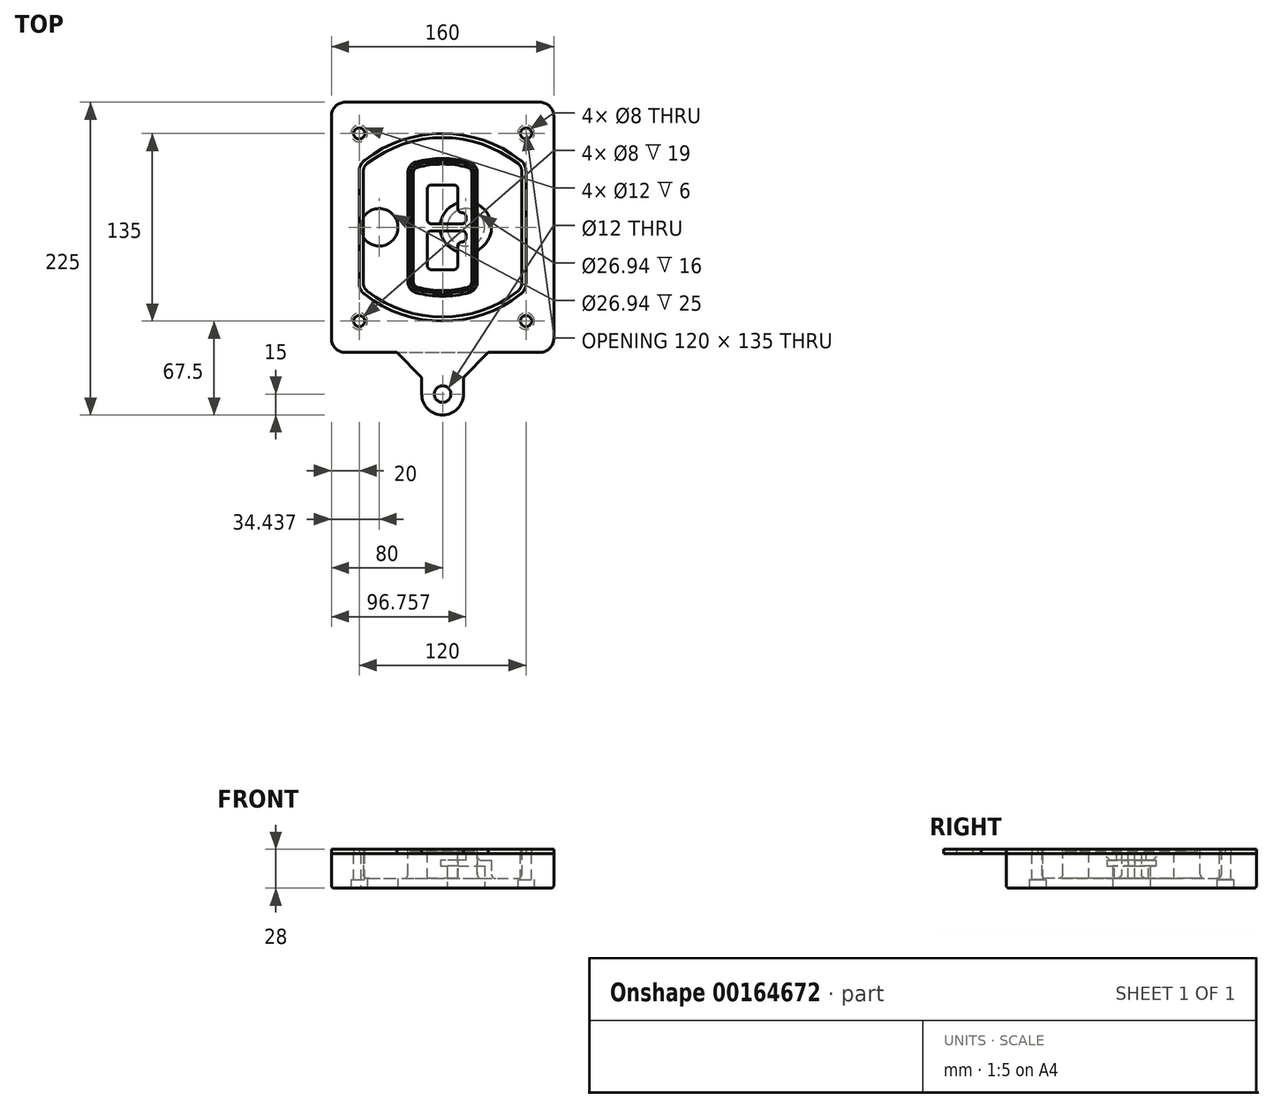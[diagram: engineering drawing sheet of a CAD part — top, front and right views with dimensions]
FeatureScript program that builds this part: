
annotation { "Feature Type Name" : "Feature", "Feature Type Description" : "" }
export const myFeature = defineFeature(function(context is Context, id is Id, definition is map)
    precondition{}
    {
        {
            var Q0;
            Q0=qCreatedBy(makeId("Top.planeOp"),FACE);
            var sketch = newSketch(context, id + "F0", { "sketchPlane" : qUnion([Q0])});
            skPoint(sketch, "E0.rect.middle", {"position": v(0, 0) * mm});
            skLineSegment(sketch, "E1.bottom", {"start": v(-70, -90) * mm, "end": v(70, -90) * mm});
            skLineSegment(sketch, "E1.top", {"start": v(-70, 90) * mm, "end": v(70, 90) * mm});
            skLineSegment(sketch, "E1.left", {"start": v(-80, -80) * mm, "end": v(-80, 80) * mm});
            skLineSegment(sketch, "E1.right", {"start": v(80, -80) * mm, "end": v(80, 80) * mm});
            skLineSegment(sketch, "E2", {"start": v(-80, 90) * mm, "end": v(80, -90) * mm, "construction": true});
            skLineSegment(sketch, "E3", {"start": v(80, 90) * mm, "end": v(-80, -90) * mm, "construction": true});
            skCircle(sketch, "E4", {"center": v(-60, 67.5) * mm, "radius": 4 * mm});
            skCircle(sketch, "E5", {"center": v(60, 67.5) * mm, "radius": 4 * mm});
            skCircle(sketch, "E6", {"center": v(60, -67.5) * mm, "radius": 4 * mm});
            skCircle(sketch, "E7", {"center": v(-60, -67.5) * mm, "radius": 4 * mm});
            skLineSegment(sketch, "E8", {"start": v(-60, 67.5) * mm, "end": v(60, 67.5) * mm, "construction": true});
            skLineSegment(sketch, "E9", {"start": v(60, 67.5) * mm, "end": v(60, -67.5) * mm, "construction": true});
            skLineSegment(sketch, "E10", {"start": v(60, -67.5) * mm, "end": v(-60, -67.5) * mm, "construction": true});
            skLineSegment(sketch, "E11", {"start": v(-60, -67.5) * mm, "end": v(-60, 67.5) * mm, "construction": true});
            skLineSegment(sketch, "E12", {"start": v(-60, 40.3) * mm, "end": v(-60, -40.3) * mm});
            skLineSegment(sketch, "E13", {"start": v(60, 40.3) * mm, "end": v(60, -40.3) * mm});
            skArc(sketch, "E14", {"start": v(56.15, 48.18) * mm, "mid": v(0, 67.5) * mm, "end": v(-56.15, 48.18) * mm});
            skArc(sketch, "E15", {"start": v(-56.15, -48.18) * mm, "mid": v(0, -67.5) * mm, "end": v(56.15, -48.18) * mm});
            skLineSegment(sketch, "E16", {"start": v(-60, 0) * mm, "end": v(60, 0) * mm, "construction": true});
            skPoint(sketch, "E17.visualSharp", {"position": v(-60, -45) * mm});
            skArc(sketch, "E17.filletArc", {"start": v(-60, -40.3) * mm, "mid": v(-58.99, -44.68) * mm, "end": v(-56.15, -48.18) * mm});
            skPoint(sketch, "E18.visualSharp", {"position": v(-60, 45) * mm});
            skArc(sketch, "E18.filletArc", {"start": v(-56.15, 48.18) * mm, "mid": v(-58.99, 44.68) * mm, "end": v(-60, 40.3) * mm});
            skPoint(sketch, "E19.visualSharp", {"position": v(60, 45) * mm});
            skArc(sketch, "E19.filletArc", {"start": v(60, 40.3) * mm, "mid": v(58.99, 44.68) * mm, "end": v(56.15, 48.18) * mm});
            skPoint(sketch, "E20.visualSharp", {"position": v(60, -45) * mm});
            skArc(sketch, "E20.filletArc", {"start": v(56.15, -48.18) * mm, "mid": v(58.99, -44.68) * mm, "end": v(60, -40.3) * mm});
            skPoint(sketch, "E21.visualSharp", {"position": v(-80, 90) * mm});
            skArc(sketch, "E21.filletArc", {"start": v(-70, 90) * mm, "mid": v(-77.07, 87.07) * mm, "end": v(-80, 80) * mm});
            skPoint(sketch, "E22.visualSharp", {"position": v(80, 90) * mm});
            skArc(sketch, "E22.filletArc", {"start": v(80, 80) * mm, "mid": v(77.07, 87.07) * mm, "end": v(70, 90) * mm});
            skPoint(sketch, "E23.visualSharp", {"position": v(80, -90) * mm});
            skArc(sketch, "E23.filletArc", {"start": v(70, -90) * mm, "mid": v(77.07, -87.07) * mm, "end": v(80, -80) * mm});
            skPoint(sketch, "E24.visualSharp", {"position": v(-80, -90) * mm});
            skArc(sketch, "E24.filletArc", {"start": v(-80, -80) * mm, "mid": v(-77.07, -87.07) * mm, "end": v(-70, -90) * mm});
            skArc(sketch, "E25.0", {"start": v(57, 40.3) * mm, "mid": v(56.3, 43.36) * mm, "end": v(54.3, 45.81) * mm});
            skLineSegment(sketch, "E25.1", {"start": v(57, 40.3) * mm, "end": v(57, -40.3) * mm});
            skArc(sketch, "E25.2", {"start": v(54.3, -45.81) * mm, "mid": v(56.3, -43.36) * mm, "end": v(57, -40.3) * mm});
            skArc(sketch, "E25.3", {"start": v(-54.3, -45.81) * mm, "mid": v(0, -64.5) * mm, "end": v(54.3, -45.81) * mm});
            skArc(sketch, "E25.4", {"start": v(-57, -40.3) * mm, "mid": v(-56.3, -43.36) * mm, "end": v(-54.3, -45.81) * mm});
            skArc(sketch, "E25.5", {"start": v(54.3, 45.81) * mm, "mid": v(0, 64.5) * mm, "end": v(-54.3, 45.81) * mm});
            skLineSegment(sketch, "E25.6", {"start": v(-57, 40.3) * mm, "end": v(-57, -40.3) * mm});
            skArc(sketch, "E25.7", {"start": v(-54.3, 45.81) * mm, "mid": v(-56.3, 43.36) * mm, "end": v(-57, 40.3) * mm});
            skArc(sketch, "E26.0", {"start": v(-58.62, 51.33) * mm, "mid": v(-62.58, 46.43) * mm, "end": v(-64, 40.3) * mm});
            skArc(sketch, "E26.1", {"start": v(58.62, 51.33) * mm, "mid": v(0, 71.5) * mm, "end": v(-58.62, 51.33) * mm});
            skArc(sketch, "E26.2", {"start": v(64, 40.3) * mm, "mid": v(62.58, 46.43) * mm, "end": v(58.62, 51.33) * mm});
            skLineSegment(sketch, "E26.3", {"start": v(64, 40.3) * mm, "end": v(64, -40.3) * mm});
            skArc(sketch, "E26.4", {"start": v(58.62, -51.33) * mm, "mid": v(62.58, -46.43) * mm, "end": v(64, -40.3) * mm});
            skLineSegment(sketch, "E26.5", {"start": v(-64, 40.3) * mm, "end": v(-64, -40.3) * mm});
            skArc(sketch, "E26.6", {"start": v(-58.62, -51.33) * mm, "mid": v(0, -71.5) * mm, "end": v(58.62, -51.33) * mm});
            skArc(sketch, "E26.7", {"start": v(-64, -40.3) * mm, "mid": v(-62.58, -46.43) * mm, "end": v(-58.62, -51.33) * mm});
            skSolve(sketch);
        }
        {
            var Q0;
            Q0=makeQuery(id+"F0.imprint","IMPRINT",FACE,{"disambiguationData":[TD([[makeQuery(id+"F0.imprint","IMPRINT",EDGE,{"derivedFrom":sQuery(id+"F0.wireOp",EDGE,"E1.bottom")}),1.0]])]});
            var Q1;
            Q1=makeQuery(id+"F0.imprint","IMPRINT",FACE,{"disambiguationData":[TD([[makeQuery(id+"F0.imprint","IMPRINT",EDGE,{"derivedFrom":sQuery(id+"F0.wireOp",EDGE,"E12")}),1.0]])]});
            var Q2;
            Q2=makeQuery(id+"F0.imprint","IMPRINT",FACE,{"disambiguationData":[TD([[makeQuery(id+"F0.imprint","IMPRINT",EDGE,{"derivedFrom":sQuery(id+"F0.wireOp",EDGE,"E25.0")}),1.0]])]});
            var Q3;
            Q3=makeQuery(id+"F0.imprint","IMPRINT",FACE,{"disambiguationData":[TD([[makeQuery(id+"F0.imprint","IMPRINT",EDGE,{"derivedFrom":sQuery(id+"F0.wireOp",EDGE,"E12")}),-1.0]])]});
            extrude(context, id + "F1", {"entities" : qUnion([Q0, Q1, Q2, Q3]), "oppositeDirection" : true, "depth" : 25 * mm});
        }
        {
            var Q0;
            Q0=makeQuery(id+"F0.imprint","IMPRINT",FACE,{"disambiguationData":[TD([[makeQuery(id+"F0.imprint","IMPRINT",EDGE,{"derivedFrom":sQuery(id+"F0.wireOp",EDGE,"E12")}),1.0]])]});
            extrude(context, id + "F2", {"entities" : qUnion([Q0]), "operationType" : NewBodyOperationType.ADD, "depth" : 3 * mm});
        }
        {
            var Q0;
            Q0=makeQuery(id+"F0.imprint","IMPRINT",FACE,{"disambiguationData":[TD([[makeQuery(id+"F0.imprint","IMPRINT",EDGE,{"derivedFrom":sQuery(id+"F0.wireOp",EDGE,"E25.0")}),1.0]])]});
            extrude(context, id + "F3", {"entities" : qUnion([Q0]), "operationType" : NewBodyOperationType.REMOVE, "oppositeDirection" : true, "depth" : 18 * mm});
        }
        {
            var Q0;
            Q0=makeQuery(id+"F2.opExtrude","CAP_FACE",FACE,{"disambiguationData":[OSD([sQuery(id+"F0.wireOp",EDGE,"E12"),sQuery(id+"F0.wireOp",EDGE,"E13"),sQuery(id+"F0.wireOp",EDGE,"E14"),sQuery(id+"F0.wireOp",EDGE,"E15"),sQuery(id+"F0.wireOp",EDGE,"E17.filletArc"),sQuery(id+"F0.wireOp",EDGE,"E18.filletArc"),sQuery(id+"F0.wireOp",EDGE,"E19.filletArc"),sQuery(id+"F0.wireOp",EDGE,"E20.filletArc"),sQuery(id+"F0.wireOp",EDGE,"E25.0"),sQuery(id+"F0.wireOp",EDGE,"E25.1"),sQuery(id+"F0.wireOp",EDGE,"E25.2"),sQuery(id+"F0.wireOp",EDGE,"E25.3"),sQuery(id+"F0.wireOp",EDGE,"E25.4"),sQuery(id+"F0.wireOp",EDGE,"E25.5"),sQuery(id+"F0.wireOp",EDGE,"E25.6"),sQuery(id+"F0.wireOp",EDGE,"E25.7")])],"isStart":false});
            var sketch = newSketch(context, id + "F4", { "sketchPlane" : qUnion([Q0])});
            skArc(sketch, "E27.0", {"start": v(-19.08, -46.97) * mm, "mid": v(0, -49.5) * mm, "end": v(19.08, -46.97) * mm});
            skArc(sketch, "E28.0", {"start": v(19.08, 46.97) * mm, "mid": v(0, 49.5) * mm, "end": v(-19.08, 46.97) * mm});
            skLineSegment(sketch, "E29", {"start": v(-25, 39.25) * mm, "end": v(-25, -39.25) * mm});
            skLineSegment(sketch, "E30", {"start": v(25, 39.25) * mm, "end": v(25, -39.25) * mm});
            skLineSegment(sketch, "E31", {"start": v(-25, 45.1) * mm, "end": v(25, 45.1) * mm, "construction": true});
            skLineSegment(sketch, "E32", {"start": v(-25, -45.1) * mm, "end": v(25, -45.1) * mm, "construction": true});
            skPoint(sketch, "E33.visualSharp", {"position": v(-25, 45.1) * mm});
            skArc(sketch, "E33.filletArc", {"start": v(-19.08, 46.97) * mm, "mid": v(-23.35, 44.11) * mm, "end": v(-25, 39.25) * mm});
            skPoint(sketch, "E34.visualSharp", {"position": v(25, 45.1) * mm});
            skArc(sketch, "E34.filletArc", {"start": v(25, 39.25) * mm, "mid": v(23.35, 44.11) * mm, "end": v(19.08, 46.97) * mm});
            skPoint(sketch, "E35.visualSharp", {"position": v(25, -45.1) * mm});
            skArc(sketch, "E35.filletArc", {"start": v(19.08, -46.97) * mm, "mid": v(23.35, -44.11) * mm, "end": v(25, -39.25) * mm});
            skPoint(sketch, "E36.visualSharp", {"position": v(-25, -45.1) * mm});
            skArc(sketch, "E36.filletArc", {"start": v(-25, -39.25) * mm, "mid": v(-23.35, -44.11) * mm, "end": v(-19.08, -46.97) * mm});
            skArc(sketch, "E37.0", {"start": v(54.3, 45.81) * mm, "mid": v(0, 64.5) * mm, "end": v(-54.3, 45.81) * mm});
            skArc(sketch, "E37.1", {"start": v(-54.3, 45.81) * mm, "mid": v(-56.3, 43.36) * mm, "end": v(-57, 40.3) * mm});
            skLineSegment(sketch, "E37.2", {"start": v(-57, 40.3) * mm, "end": v(-57, -40.3) * mm});
            skArc(sketch, "E37.3", {"start": v(-57, -40.3) * mm, "mid": v(-56.3, -43.36) * mm, "end": v(-54.3, -45.81) * mm});
            skArc(sketch, "E37.4", {"start": v(-54.3, -45.81) * mm, "mid": v(0, -64.5) * mm, "end": v(54.3, -45.81) * mm});
            skArc(sketch, "E37.5", {"start": v(54.3, -45.81) * mm, "mid": v(56.3, -43.36) * mm, "end": v(57, -40.3) * mm});
            skLineSegment(sketch, "E37.6", {"start": v(57, 40.3) * mm, "end": v(57, -40.3) * mm});
            skArc(sketch, "E37.7", {"start": v(57, 40.3) * mm, "mid": v(56.3, 43.36) * mm, "end": v(54.3, 45.81) * mm});
            skLineSegment(sketch, "E38.0", {"start": v(23, 39.25) * mm, "end": v(23, -39.25) * mm});
            skArc(sketch, "E38.1", {"start": v(18.56, -45.04) * mm, "mid": v(21.76, -42.9) * mm, "end": v(23, -39.25) * mm});
            skArc(sketch, "E38.2", {"start": v(-18.56, -45.04) * mm, "mid": v(0, -47.5) * mm, "end": v(18.56, -45.04) * mm});
            skArc(sketch, "E38.3", {"start": v(-23, -39.25) * mm, "mid": v(-21.76, -42.9) * mm, "end": v(-18.56, -45.04) * mm});
            skLineSegment(sketch, "E38.4", {"start": v(-23, 39.25) * mm, "end": v(-23, -39.25) * mm});
            skArc(sketch, "E38.5", {"start": v(23, 39.25) * mm, "mid": v(21.76, 42.9) * mm, "end": v(18.56, 45.04) * mm});
            skArc(sketch, "E38.6", {"start": v(-18.56, 45.04) * mm, "mid": v(-21.76, 42.9) * mm, "end": v(-23, 39.25) * mm});
            skArc(sketch, "E38.7", {"start": v(18.56, 45.04) * mm, "mid": v(0, 47.5) * mm, "end": v(-18.56, 45.04) * mm});
            skArc(sketch, "E39.0", {"start": v(21, 39.25) * mm, "mid": v(20.18, 41.68) * mm, "end": v(18.04, 43.1) * mm});
            skLineSegment(sketch, "E39.1", {"start": v(21, 39.25) * mm, "end": v(21, -39.25) * mm});
            skArc(sketch, "E39.2", {"start": v(18.04, -43.1) * mm, "mid": v(20.18, -41.68) * mm, "end": v(21, -39.25) * mm});
            skArc(sketch, "E39.3", {"start": v(-18.04, -43.1) * mm, "mid": v(0, -45.5) * mm, "end": v(18.04, -43.1) * mm});
            skArc(sketch, "E39.4", {"start": v(-21, -39.25) * mm, "mid": v(-20.18, -41.68) * mm, "end": v(-18.04, -43.1) * mm});
            skArc(sketch, "E39.5", {"start": v(18.04, 43.1) * mm, "mid": v(0, 45.5) * mm, "end": v(-18.04, 43.1) * mm});
            skLineSegment(sketch, "E39.6", {"start": v(-21, 39.25) * mm, "end": v(-21, -39.25) * mm});
            skArc(sketch, "E39.7", {"start": v(-18.04, 43.1) * mm, "mid": v(-20.18, 41.68) * mm, "end": v(-21, 39.25) * mm});
            skLineSegment(sketch, "E40", {"start": v(-25, 0) * mm, "end": v(25, 0) * mm, "construction": true});
            skLineSegment(sketch, "E41", {"start": v(-11, 5.5) * mm, "end": v(-11, 27.5) * mm});
            skLineSegment(sketch, "E42", {"start": v(-8, 30.5) * mm, "end": v(8, 30.5) * mm});
            skLineSegment(sketch, "E43", {"start": v(11, 27.5) * mm, "end": v(11, 13.5) * mm});
            skLineSegment(sketch, "E44", {"start": v(14, 10.5) * mm, "end": v(14, 10.5) * mm});
            skLineSegment(sketch, "E45", {"start": v(17, 7.5) * mm, "end": v(17, 5.5) * mm});
            skLineSegment(sketch, "E46", {"start": v(14, 2.5) * mm, "end": v(-8, 2.5) * mm});
            skPoint(sketch, "E47.visualSharp", {"position": v(-11, 30.5) * mm});
            skArc(sketch, "E47.filletArc", {"start": v(-8, 30.5) * mm, "mid": v(-10.12, 29.62) * mm, "end": v(-11, 27.5) * mm});
            skPoint(sketch, "E48.visualSharp", {"position": v(11, 30.5) * mm});
            skArc(sketch, "E48.filletArc", {"start": v(11, 27.5) * mm, "mid": v(10.12, 29.62) * mm, "end": v(8, 30.5) * mm});
            skPoint(sketch, "E49.visualSharp", {"position": v(11, 10.5) * mm});
            skArc(sketch, "E49.filletArc", {"start": v(11, 13.5) * mm, "mid": v(11.88, 11.38) * mm, "end": v(14, 10.5) * mm});
            skPoint(sketch, "E50.visualSharp", {"position": v(17, 10.5) * mm});
            skArc(sketch, "E50.filletArc", {"start": v(17, 7.5) * mm, "mid": v(16.12, 9.62) * mm, "end": v(14, 10.5) * mm});
            skPoint(sketch, "E51.visualSharp", {"position": v(17, 2.5) * mm});
            skArc(sketch, "E51.filletArc", {"start": v(14, 2.5) * mm, "mid": v(16.12, 3.38) * mm, "end": v(17, 5.5) * mm});
            skPoint(sketch, "E52.visualSharp", {"position": v(-11, 2.5) * mm});
            skArc(sketch, "E52.filletArc", {"start": v(-11, 5.5) * mm, "mid": v(-10.12, 3.38) * mm, "end": v(-8, 2.5) * mm});
            skLineSegment(sketch, "E53.0.MirrorCS", {"start": v(14, -2.5) * mm, "end": v(-8, -2.5) * mm});
            skArc(sketch, "E54.0.MirrorCS", {"start": v(-11, -5.5) * mm, "mid": v(-10.12, -3.38) * mm, "end": v(-8, -2.5) * mm});
            skLineSegment(sketch, "E55.0.MirrorCS", {"start": v(-11, -5.5) * mm, "end": v(-11, -27.5) * mm});
            skArc(sketch, "E56.0.MirrorCS", {"start": v(-8, -30.5) * mm, "mid": v(-10.12, -29.62) * mm, "end": v(-11, -27.5) * mm});
            skLineSegment(sketch, "E57.0.MirrorCS", {"start": v(-8, -30.5) * mm, "end": v(8, -30.5) * mm});
            skArc(sketch, "E58.0.MirrorCS", {"start": v(11, -27.5) * mm, "mid": v(10.12, -29.62) * mm, "end": v(8, -30.5) * mm});
            skLineSegment(sketch, "E59.0.MirrorCS", {"start": v(11, -27.5) * mm, "end": v(11, -13.5) * mm});
            skArc(sketch, "E60.0.MirrorCS", {"start": v(11, -13.5) * mm, "mid": v(11.88, -11.38) * mm, "end": v(14, -10.5) * mm});
            skArc(sketch, "E61.0.MirrorCS", {"start": v(17, -7.5) * mm, "mid": v(16.12, -9.62) * mm, "end": v(14, -10.5) * mm});
            skLineSegment(sketch, "E62.0.MirrorCS", {"start": v(17, -7.5) * mm, "end": v(17, -5.5) * mm});
            skArc(sketch, "E63.0.MirrorCS", {"start": v(14, -2.5) * mm, "mid": v(16.12, -3.38) * mm, "end": v(17, -5.5) * mm});
            skSolve(sketch);
        }
        {
            var Q0;
            Q0=makeQuery(id+"F4.imprint","IMPRINT",FACE,{"disambiguationData":[TD([[makeQuery(id+"F4.imprint","IMPRINT",EDGE,{"derivedFrom":sQuery(id+"F4.wireOp",EDGE,"E27.0")}),1.0]])]});
            var Q1;
            Q1=makeQuery(id+"F4.imprint","IMPRINT",FACE,{"disambiguationData":[TD([[makeQuery(id+"F4.imprint","IMPRINT",EDGE,{"derivedFrom":sQuery(id+"F4.wireOp",EDGE,"E38.0")}),-1.0]])]});
            var Q2;
            Q2=makeQuery(id+"F4.imprint","IMPRINT",FACE,{"disambiguationData":[TD([[makeQuery(id+"F4.imprint","IMPRINT",EDGE,{"derivedFrom":sQuery(id+"F4.wireOp",EDGE,"E39.0")}),1.0]])]});
            extrude(context, id + "F5", {"entities" : qUnion([Q0, Q1, Q2]), "operationType" : NewBodyOperationType.ADD, "endBound" : BoundingType.UP_TO_NEXT, "oppositeDirection" : true, "depth" : 25 * mm});
        }
        {
            var Q0;
            Q0=makeQuery(id+"F4.imprint","IMPRINT",FACE,{"disambiguationData":[TD([[makeQuery(id+"F4.imprint","IMPRINT",EDGE,{"derivedFrom":sQuery(id+"F4.wireOp",EDGE,"E38.0")}),-1.0]])]});
            extrude(context, id + "F6", {"entities" : qUnion([Q0]), "operationType" : NewBodyOperationType.REMOVE, "oppositeDirection" : true, "depth" : 2 * mm});
        }
        {
            var Q0;
            Q0=makeQuery(id+"F1.opExtrude","CAP_FACE",FACE,{"disambiguationData":[OSD([sQuery(id+"F0.wireOp",EDGE,"E1.bottom"),sQuery(id+"F0.wireOp",EDGE,"E1.top"),sQuery(id+"F0.wireOp",EDGE,"E1.left"),sQuery(id+"F0.wireOp",EDGE,"E1.right"),sQuery(id+"F0.wireOp",EDGE,"E4"),sQuery(id+"F0.wireOp",EDGE,"E5"),sQuery(id+"F0.wireOp",EDGE,"E6"),sQuery(id+"F0.wireOp",EDGE,"E7"),sQuery(id+"F0.wireOp",EDGE,"E21.filletArc"),sQuery(id+"F0.wireOp",EDGE,"E22.filletArc"),sQuery(id+"F0.wireOp",EDGE,"E23.filletArc"),sQuery(id+"F0.wireOp",EDGE,"E24.filletArc")])],"isStart":false});
            var sketch = newSketch(context, id + "F7", { "sketchPlane" : qUnion([Q0])});
            skCircle(sketch, "E64", {"center": v(16.76, 0) * mm, "radius": 13.47 * mm});
            skCircle(sketch, "E65", {"center": v(-45.56, 0) * mm, "radius": 13.47 * mm});
            skLineSegment(sketch, "E66", {"start": v(80, 0) * mm, "end": v(-80, 0) * mm});
            skCircle(sketch, "E67", {"center": v(16.76, 0) * mm, "radius": 18.47 * mm});
            skCircle(sketch, "E68", {"center": v(60, -67.5) * mm, "radius": 6 * mm});
            skCircle(sketch, "E69", {"center": v(-60, -67.5) * mm, "radius": 6 * mm});
            skCircle(sketch, "E70", {"center": v(-60, 67.5) * mm, "radius": 6 * mm});
            skCircle(sketch, "E71", {"center": v(60, 67.5) * mm, "radius": 6 * mm});
            skSolve(sketch);
        }
        {
            var Q0;
            {var subQ1=sQuery(id+"F7.wireOp",EDGE,"E66");var subQ4=sQuery(id+"F7.wireOp",EDGE,"E64");var subQ6=makeQuery(id+"F7.imprint","INTERSECT",VERTEX,{"disambiguationData":[OD(0.0)],"derivedFrom":[subQ4,subQ1]});Q0=makeQuery(id+"F7.imprint","IMPRINT",FACE,{"disambiguationData":[TD([[makeQuery(id+"F7.imprint","IMPRINT",EDGE,{"disambiguationData":[TD([[subQ6,-1.0]])],"derivedFrom":subQ4}),-1.0]])]});}
            var Q1;
            {var subQ0=sQuery(id+"F7.wireOp",EDGE,"E66");var subQ1=sQuery(id+"F7.wireOp",EDGE,"E64");var subQ3=makeQuery(id+"F7.imprint","INTERSECT",VERTEX,{"disambiguationData":[OD(0.0)],"derivedFrom":[subQ1,subQ0]});Q1=makeQuery(id+"F7.imprint","IMPRINT",FACE,{"disambiguationData":[TD([[makeQuery(id+"F7.imprint","IMPRINT",EDGE,{"disambiguationData":[TD([[subQ3,-1.0]])],"derivedFrom":subQ1}),1.0]])]});}
            var Q2;
            {var subQ0=sQuery(id+"F7.wireOp",EDGE,"E66");var subQ1=sQuery(id+"F7.wireOp",EDGE,"E64");var subQ3=makeQuery(id+"F7.imprint","INTERSECT",VERTEX,{"disambiguationData":[OD(0.0)],"derivedFrom":[subQ1,subQ0]});Q2=makeQuery(id+"F7.imprint","IMPRINT",FACE,{"disambiguationData":[TD([[makeQuery(id+"F7.imprint","IMPRINT",EDGE,{"disambiguationData":[TD([[subQ3,1.0]])],"derivedFrom":subQ1}),1.0]])]});}
            var Q3;
            {var subQ1=sQuery(id+"F7.wireOp",EDGE,"E66");var subQ4=sQuery(id+"F7.wireOp",EDGE,"E64");var subQ6=makeQuery(id+"F7.imprint","INTERSECT",VERTEX,{"disambiguationData":[OD(0.0)],"derivedFrom":[subQ4,subQ1]});Q3=makeQuery(id+"F7.imprint","IMPRINT",FACE,{"disambiguationData":[TD([[makeQuery(id+"F7.imprint","IMPRINT",EDGE,{"disambiguationData":[TD([[subQ6,1.0]])],"derivedFrom":subQ4}),-1.0]])]});}
            extrude(context, id + "F8", {"entities" : qUnion([Q0, Q1, Q2, Q3]), "operationType" : NewBodyOperationType.ADD, "oppositeDirection" : true, "depth" : 20 * mm});
        }
        {
            var Q0;
            {var subQ0=sQuery(id+"F7.wireOp",EDGE,"E66");var subQ1=sQuery(id+"F7.wireOp",EDGE,"E64");var subQ3=makeQuery(id+"F7.imprint","INTERSECT",VERTEX,{"disambiguationData":[OD(0.0)],"derivedFrom":[subQ1,subQ0]});Q0=makeQuery(id+"F7.imprint","IMPRINT",FACE,{"disambiguationData":[TD([[makeQuery(id+"F7.imprint","IMPRINT",EDGE,{"disambiguationData":[TD([[subQ3,-1.0]])],"derivedFrom":subQ1}),1.0]])]});}
            var Q1;
            {var subQ0=sQuery(id+"F7.wireOp",EDGE,"E66");var subQ1=sQuery(id+"F7.wireOp",EDGE,"E64");var subQ3=makeQuery(id+"F7.imprint","INTERSECT",VERTEX,{"disambiguationData":[OD(0.0)],"derivedFrom":[subQ1,subQ0]});Q1=makeQuery(id+"F7.imprint","IMPRINT",FACE,{"disambiguationData":[TD([[makeQuery(id+"F7.imprint","IMPRINT",EDGE,{"disambiguationData":[TD([[subQ3,1.0]])],"derivedFrom":subQ1}),1.0]])]});}
            extrude(context, id + "F9", {"entities" : qUnion([Q0, Q1]), "operationType" : NewBodyOperationType.REMOVE, "oppositeDirection" : true, "depth" : 16 * mm});
        }
        {
            var Q0;
            {var subQ0=sQuery(id+"F7.wireOp",EDGE,"E66");var subQ1=sQuery(id+"F7.wireOp",EDGE,"E65");var subQ3=makeQuery(id+"F7.imprint","INTERSECT",VERTEX,{"disambiguationData":[OD(0.0)],"derivedFrom":[subQ1,subQ0]});Q0=makeQuery(id+"F7.imprint","IMPRINT",FACE,{"disambiguationData":[TD([[makeQuery(id+"F7.imprint","IMPRINT",EDGE,{"disambiguationData":[TD([[subQ3,-1.0]])],"derivedFrom":subQ1}),1.0]])]});}
            var Q1;
            {var subQ0=sQuery(id+"F7.wireOp",EDGE,"E66");var subQ1=sQuery(id+"F7.wireOp",EDGE,"E65");var subQ3=makeQuery(id+"F7.imprint","INTERSECT",VERTEX,{"disambiguationData":[OD(0.0)],"derivedFrom":[subQ1,subQ0]});Q1=makeQuery(id+"F7.imprint","IMPRINT",FACE,{"disambiguationData":[TD([[makeQuery(id+"F7.imprint","IMPRINT",EDGE,{"disambiguationData":[TD([[subQ3,1.0]])],"derivedFrom":subQ1}),1.0]])]});}
            extrude(context, id + "F10", {"entities" : qUnion([Q0, Q1]), "operationType" : NewBodyOperationType.REMOVE, "oppositeDirection" : true, "depth" : 25 * mm});
        }
        {
            var Q0;
            Q0=makeQuery(id+"F7.imprint","IMPRINT",FACE,{"disambiguationData":[TD([[makeQuery(id+"F7.imprint","IMPRINT",EDGE,{"derivedFrom":sQuery(id+"F7.wireOp",EDGE,"E68")}),1.0]])]});
            var Q1;
            Q1=makeQuery(id+"F7.imprint","IMPRINT",FACE,{"disambiguationData":[TD([[makeQuery(id+"F7.imprint","IMPRINT",EDGE,{"derivedFrom":makeQuery(id+"F1.opExtrude","CAP_EDGE",EDGE,{"disambiguationData":[OSD([sQuery(id+"F0.wireOp",EDGE,"E5")])],"isStart":false})}),-1.0]])]});
            var Q2;
            Q2=makeQuery(id+"F7.imprint","IMPRINT",FACE,{"disambiguationData":[TD([[makeQuery(id+"F7.imprint","IMPRINT",EDGE,{"derivedFrom":sQuery(id+"F7.wireOp",EDGE,"E69")}),1.0]])]});
            var Q3;
            Q3=makeQuery(id+"F7.imprint","IMPRINT",FACE,{"disambiguationData":[TD([[makeQuery(id+"F7.imprint","IMPRINT",EDGE,{"derivedFrom":makeQuery(id+"F1.opExtrude","CAP_EDGE",EDGE,{"disambiguationData":[OSD([sQuery(id+"F0.wireOp",EDGE,"E4")])],"isStart":false})}),-1.0]])]});
            var Q4;
            Q4=makeQuery(id+"F7.imprint","IMPRINT",FACE,{"disambiguationData":[TD([[makeQuery(id+"F7.imprint","IMPRINT",EDGE,{"derivedFrom":sQuery(id+"F7.wireOp",EDGE,"E70")}),1.0]])]});
            var Q5;
            Q5=makeQuery(id+"F7.imprint","IMPRINT",FACE,{"disambiguationData":[TD([[makeQuery(id+"F7.imprint","IMPRINT",EDGE,{"derivedFrom":makeQuery(id+"F1.opExtrude","CAP_EDGE",EDGE,{"disambiguationData":[OSD([sQuery(id+"F0.wireOp",EDGE,"E7")])],"isStart":false})}),-1.0]])]});
            var Q6;
            Q6=makeQuery(id+"F7.imprint","IMPRINT",FACE,{"disambiguationData":[TD([[makeQuery(id+"F7.imprint","IMPRINT",EDGE,{"derivedFrom":sQuery(id+"F7.wireOp",EDGE,"E71")}),1.0]])]});
            var Q7;
            Q7=makeQuery(id+"F7.imprint","IMPRINT",FACE,{"disambiguationData":[TD([[makeQuery(id+"F7.imprint","IMPRINT",EDGE,{"derivedFrom":makeQuery(id+"F1.opExtrude","CAP_EDGE",EDGE,{"disambiguationData":[OSD([sQuery(id+"F0.wireOp",EDGE,"E6")])],"isStart":false})}),-1.0]])]});
            extrude(context, id + "F11", {"entities" : qUnion([Q0, Q1, Q2, Q3, Q4, Q5, Q6, Q7]), "operationType" : NewBodyOperationType.REMOVE, "oppositeDirection" : true, "depth" : 6 * mm});
        }
        {
            var Q0;
            Q0=makeQuery(id+"F9.boolean.opBoolean","COPY",FACE,{"derivedFrom":makeQuery(id+"F9.opExtrude","CAP_FACE",FACE,{"disambiguationData":[OSD([sQuery(id+"F7.wireOp",EDGE,"E64")])],"isStart":false})});
            var sketch = newSketch(context, id + "F12", { "sketchPlane" : qUnion([Q0])});
            skArc(sketch, "E72.0", {"start": v(11, 17.55) * mm, "mid": v(2.57, 11.82) * mm, "end": v(-1.54, 2.5) * mm});
            skArc(sketch, "E72.1", {"start": v(-1.54, -2.5) * mm, "mid": v(2.57, -11.82) * mm, "end": v(11, -17.55) * mm});
            skLineSegment(sketch, "E73", {"start": v(-1.54, -2.5) * mm, "end": v(14, -2.5) * mm});
            skLineSegment(sketch, "E74.0", {"start": v(14, 2.5) * mm, "end": v(-1.54, 2.5) * mm});
            skArc(sketch, "E74.1", {"start": v(14, 2.5) * mm, "mid": v(16.12, 3.38) * mm, "end": v(17, 5.5) * mm});
            skLineSegment(sketch, "E74.2", {"start": v(17, 7.5) * mm, "end": v(17, 5.5) * mm});
            skArc(sketch, "E74.3", {"start": v(17, 7.5) * mm, "mid": v(16.12, 9.62) * mm, "end": v(14, 10.5) * mm});
            skArc(sketch, "E74.4", {"start": v(11, 13.5) * mm, "mid": v(11.88, 11.38) * mm, "end": v(14, 10.5) * mm});
            skLineSegment(sketch, "E74.5", {"start": v(11, 17.55) * mm, "end": v(11, 13.5) * mm});
            skLineSegment(sketch, "E74.7", {"start": v(14, -2.5) * mm, "end": v(-1.54, -2.5) * mm});
            skArc(sketch, "E74.8", {"start": v(14, -2.5) * mm, "mid": v(16.12, -3.38) * mm, "end": v(17, -5.5) * mm});
            skLineSegment(sketch, "E74.9", {"start": v(17, -7.5) * mm, "end": v(17, -5.5) * mm});
            skArc(sketch, "E74.10", {"start": v(17, -7.5) * mm, "mid": v(16.12, -9.62) * mm, "end": v(14, -10.5) * mm});
            skArc(sketch, "E74.11", {"start": v(11, -13.5) * mm, "mid": v(11.88, -11.38) * mm, "end": v(14, -10.5) * mm});
            skLineSegment(sketch, "E74.12", {"start": v(11, -17.55) * mm, "end": v(11, -13.5) * mm});
            skPoint(sketch, "E75.orphan", {"position": v(11, -27.5) * mm});
            skPoint(sketch, "E76.orphan", {"position": v(-8, -2.5) * mm});
            skPoint(sketch, "E77.orphan", {"position": v(-8, 2.5) * mm});
            skPoint(sketch, "E78.orphan", {"position": v(11, 27.5) * mm});
            skSolve(sketch);
        }
        {
            var Q0;
            {var subQ7=sQuery(id+"F12.wireOp",EDGE,"E72.0");var subQ14=sQuery(id+"F12.wireOp",EDGE,"E72.1");var subQ16=sQuery(id+"F12.wireOp",EDGE,"E74.1");var subQ18=sQuery(id+"F12.wireOp",EDGE,"E74.8");Q0=qUnion([makeQuery(id+"F12.imprint","IMPRINT",FACE,{"disambiguationData":[TD([[makeQuery(id+"F12.imprint","IMPRINT",EDGE,{"derivedFrom":subQ7}),1.0]])]}),makeQuery(id+"F12.imprint","IMPRINT",FACE,{"disambiguationData":[TD([[makeQuery(id+"F12.imprint","IMPRINT",EDGE,{"derivedFrom":subQ14}),1.0]])]}),makeQuery(id+"F12.imprint","IMPRINT",FACE,{"disambiguationData":[TD([[makeQuery(id+"F12.imprint","IMPRINT",EDGE,{"derivedFrom":subQ16}),1.0]])]}),makeQuery(id+"F12.imprint","IMPRINT",FACE,{"disambiguationData":[TD([[makeQuery(id+"F12.imprint","IMPRINT",EDGE,{"derivedFrom":subQ18}),-1.0]])]})]);}
            var Q1;
            Q1=makeQuery(id+"F5.boolean.opBoolean","SPLIT",FACE,{"disambiguationData":[TD([makeQuery(id+"F5.opExtrude","SWEPT_FACE",FACE,{"disambiguationData":[OSD([sQuery(id+"F4.wireOp",EDGE,"E41")])]})])],"derivedFrom":makeQuery(id+"F3.boolean.opBoolean","COPY",FACE,{"derivedFrom":makeQuery(id+"F3.opExtrude","CAP_FACE",FACE,{"disambiguationData":[OSD([sQuery(id+"F0.wireOp",EDGE,"E25.0"),sQuery(id+"F0.wireOp",EDGE,"E25.1"),sQuery(id+"F0.wireOp",EDGE,"E25.2"),sQuery(id+"F0.wireOp",EDGE,"E25.3"),sQuery(id+"F0.wireOp",EDGE,"E25.4"),sQuery(id+"F0.wireOp",EDGE,"E25.5"),sQuery(id+"F0.wireOp",EDGE,"E25.6"),sQuery(id+"F0.wireOp",EDGE,"E25.7")])],"isStart":false})})});
            extrude(context, id + "F13", {"entities" : qUnion([Q0]), "operationType" : NewBodyOperationType.REMOVE, "endBound" : BoundingType.UP_TO_SURFACE, "endBoundEntityFace" : qUnion([Q1]), "depth" : 25 * mm});
        }
        {
            var Q0;
            Q0=makeQuery(id+"F3.boolean.opBoolean","COPY",EDGE,{"derivedFrom":makeQuery(id+"F3.opExtrude","CAP_EDGE",EDGE,{"disambiguationData":[OSD([sQuery(id+"F0.wireOp",EDGE,"E25.6")])],"isStart":false})});
            var Q1;
            Q1=makeQuery(id+"F8.boolean.opBoolean","INTERSECT",EDGE,{"derivedFrom":[makeQuery(id+"F5.opExtrude","SWEPT_FACE",FACE,{"disambiguationData":[OSD([sQuery(id+"F4.wireOp",EDGE,"E30")])]}),makeQuery(id+"F8.opExtrude","CAP_FACE",FACE,{"disambiguationData":[OSD([sQuery(id+"F7.wireOp",EDGE,"E67")])],"isStart":false})]});
            var Q2;
            Q2=makeQuery(id+"F8.boolean.opBoolean","INTERSECT",EDGE,{"disambiguationData":[OD(1.0)],"derivedFrom":[makeQuery(id+"F5.opExtrude","SWEPT_FACE",FACE,{"disambiguationData":[OSD([sQuery(id+"F4.wireOp",EDGE,"E30")])]}),makeQuery(id+"F8.opExtrude","SWEPT_FACE",FACE,{"disambiguationData":[OSD([sQuery(id+"F7.wireOp",EDGE,"E67")])]})]});
            var Q3;
            {var subQ0=sQuery(id+"F4.wireOp",EDGE,"E30");Q3=makeQuery(id+"F8.boolean.opBoolean","SPLIT",EDGE,{"disambiguationData":[TD([makeQuery(id+"F5.opExtrude","SWEPT_FACE",FACE,{"disambiguationData":[OSD([sQuery(id+"F4.wireOp",EDGE,"E35.filletArc")])]})])],"derivedFrom":makeQuery(id+"F5.opExtrude","CAP_EDGE",EDGE,{"disambiguationData":[OSD([subQ0])],"isStart":false})});}
            var Q4;
            {var subQ0=sQuery(id+"F0.wireOp",EDGE,"E25.7");var subQ1=sQuery(id+"F0.wireOp",EDGE,"E25.1");var subQ2=sQuery(id+"F0.wireOp",EDGE,"E25.6");var subQ3=sQuery(id+"F0.wireOp",EDGE,"E25.5");var subQ4=sQuery(id+"F0.wireOp",EDGE,"E25.4");var subQ5=sQuery(id+"F0.wireOp",EDGE,"E25.0");var subQ6=sQuery(id+"F0.wireOp",EDGE,"E25.2");var subQ7=sQuery(id+"F0.wireOp",EDGE,"E25.3");Q4=makeQuery(id+"F8.boolean.opBoolean","INTERSECT",EDGE,{"derivedFrom":[makeQuery(id+"F5.boolean.opBoolean","SPLIT",FACE,{"disambiguationData":[TD([makeQuery(id+"F2.opExtrude","SWEPT_FACE",FACE,{"disambiguationData":[OSD([subQ5])]})])],"derivedFrom":makeQuery(id+"F3.boolean.opBoolean","COPY",FACE,{"derivedFrom":makeQuery(id+"F3.opExtrude","CAP_FACE",FACE,{"disambiguationData":[OSD([subQ5,subQ1,subQ6,subQ7,subQ4,subQ3,subQ2,subQ0])],"isStart":false})})}),makeQuery(id+"F8.opExtrude","SWEPT_FACE",FACE,{"disambiguationData":[OSD([sQuery(id+"F7.wireOp",EDGE,"E67")])]})]});}
            var Q5;
            Q5=makeQuery(id+"F8.boolean.opBoolean","INTERSECT",EDGE,{"disambiguationData":[OD(0.0)],"derivedFrom":[makeQuery(id+"F5.opExtrude","SWEPT_FACE",FACE,{"disambiguationData":[OSD([sQuery(id+"F4.wireOp",EDGE,"E30")])]}),makeQuery(id+"F8.opExtrude","SWEPT_FACE",FACE,{"disambiguationData":[OSD([sQuery(id+"F7.wireOp",EDGE,"E67")])]})]});
            fillet(context, id + "F14", {"entities" : qUnion([Q0, Q1, Q2, Q3, Q4, Q5]), "radius" : 3 * mm, "tangentPropagation" : true, "allowEdgeOverflow" : false});
        }
        {
            var Q0;
            Q0=makeQuery(id+"F1.opExtrude","CAP_EDGE",EDGE,{"disambiguationData":[OSD([sQuery(id+"F0.wireOp",EDGE,"E1.bottom")])],"isStart":false});
            fillet(context, id + "F15", {"entities" : qUnion([Q0]), "radius" : 2 * mm, "tangentPropagation" : true, "allowEdgeOverflow" : false});
        }
        {
            var Q0;
            {var subQ0=sQuery(id+"F0.wireOp",EDGE,"E22.filletArc");var subQ1=sQuery(id+"F0.wireOp",EDGE,"E7");var subQ2=sQuery(id+"F0.wireOp",EDGE,"E6");var subQ3=sQuery(id+"F0.wireOp",EDGE,"E5");var subQ4=sQuery(id+"F0.wireOp",EDGE,"E4");var subQ5=sQuery(id+"F0.wireOp",EDGE,"E1.bottom");var subQ6=sQuery(id+"F0.wireOp",EDGE,"E21.filletArc");var subQ7=sQuery(id+"F0.wireOp",EDGE,"E1.top");var subQ8=sQuery(id+"F0.wireOp",EDGE,"E1.left");var subQ9=sQuery(id+"F0.wireOp",EDGE,"E1.right");var subQ10=sQuery(id+"F0.wireOp",EDGE,"E23.filletArc");var subQ11=sQuery(id+"F0.wireOp",EDGE,"E24.filletArc");Q0=makeQuery(id+"F2.boolean.opBoolean","SPLIT",FACE,{"disambiguationData":[TD([makeQuery(id+"F1.opExtrude","SWEPT_FACE",FACE,{"disambiguationData":[OSD([subQ5])]})])],"derivedFrom":makeQuery(id+"F1.opExtrude","CAP_FACE",FACE,{"disambiguationData":[OSD([subQ5,subQ7,subQ8,subQ9,subQ4,subQ3,subQ2,subQ1,subQ6,subQ0,subQ10,subQ11])],"isStart":true})});}
            var sketch = newSketch(context, id + "F16", { "sketchPlane" : qUnion([Q0])});
            skLineSegment(sketch, "E79.0", {"start": v(-80, -80) * mm, "end": v(-80, 80) * mm});
            skArc(sketch, "E79.1", {"start": v(-80, -80) * mm, "mid": v(-77.07, -87.07) * mm, "end": v(-70, -90) * mm});
            skLineSegment(sketch, "E79.2", {"start": v(-70, -90) * mm, "end": v(70, -90) * mm});
            skArc(sketch, "E79.3", {"start": v(70, -90) * mm, "mid": v(77.07, -87.07) * mm, "end": v(80, -80) * mm});
            skLineSegment(sketch, "E79.4", {"start": v(80, -80) * mm, "end": v(80, 80) * mm});
            skArc(sketch, "E79.5", {"start": v(80, 80) * mm, "mid": v(77.07, 87.07) * mm, "end": v(70, 90) * mm});
            skLineSegment(sketch, "E79.6", {"start": v(-70, 90) * mm, "end": v(70, 90) * mm});
            skArc(sketch, "E79.7", {"start": v(-70, 90) * mm, "mid": v(-77.07, 87.07) * mm, "end": v(-80, 80) * mm});
            skArc(sketch, "E79.8", {"start": v(56.15, 48.18) * mm, "mid": v(0, 67.5) * mm, "end": v(-56.15, 48.18) * mm});
            skArc(sketch, "E79.9", {"start": v(-56.15, 48.18) * mm, "mid": v(-58.99, 44.68) * mm, "end": v(-60, 40.3) * mm});
            skLineSegment(sketch, "E79.10", {"start": v(-60, 40.3) * mm, "end": v(-60, -40.3) * mm});
            skArc(sketch, "E79.11", {"start": v(-60, -40.3) * mm, "mid": v(-58.99, -44.68) * mm, "end": v(-56.15, -48.18) * mm});
            skArc(sketch, "E79.12", {"start": v(-56.15, -48.18) * mm, "mid": v(0, -67.5) * mm, "end": v(56.15, -48.18) * mm});
            skArc(sketch, "E79.13", {"start": v(56.15, -48.18) * mm, "mid": v(58.99, -44.68) * mm, "end": v(60, -40.3) * mm});
            skLineSegment(sketch, "E79.14", {"start": v(60, 40.3) * mm, "end": v(60, -40.3) * mm});
            skArc(sketch, "E79.15", {"start": v(60, 40.3) * mm, "mid": v(58.99, 44.68) * mm, "end": v(56.15, 48.18) * mm});
            skLineSegment(sketch, "E80", {"start": v(0, 90) * mm, "end": v(0, 120) * mm, "construction": true});
            skCircle(sketch, "E81", {"center": v(0, 120) * mm, "radius": 6 * mm});
            skArc(sketch, "E82", {"start": v(-15, 120) * mm, "mid": v(0, 135) * mm, "end": v(15, 120) * mm});
            skLineSegment(sketch, "E83", {"start": v(-15, 120) * mm, "end": v(-15, 108) * mm});
            skLineSegment(sketch, "E84", {"start": v(-15, 108) * mm, "end": v(-33, 90) * mm});
            skLineSegment(sketch, "E85", {"start": v(15, 120) * mm, "end": v(15, 108) * mm});
            skLineSegment(sketch, "E86", {"start": v(15, 108) * mm, "end": v(33, 90) * mm});
            skLineSegment(sketch, "E87", {"start": v(-80, 0) * mm, "end": v(80, 0) * mm, "construction": true});
            skArc(sketch, "E88.MirrorCS", {"start": v(15, 120) * mm, "mid": v(0, 135) * mm, "end": v(-15, 120) * mm});
            skArc(sketch, "E89.MirrorCS", {"start": v(-15, -120) * mm, "mid": v(0, -135) * mm, "end": v(15, -120) * mm});
            skLineSegment(sketch, "E90.MirrorCS", {"start": v(-15, -120) * mm, "end": v(-15, -108) * mm});
            skLineSegment(sketch, "E91.MirrorCS", {"start": v(15, -120) * mm, "end": v(15, -108) * mm});
            skLineSegment(sketch, "E92.MirrorCS", {"start": v(15, -108) * mm, "end": v(33, -90) * mm});
            skCircle(sketch, "E93.MirrorC", {"center": v(0, -120) * mm, "radius": 6 * mm});
            skLineSegment(sketch, "E94.MirrorCS", {"start": v(-15, -108) * mm, "end": v(-33, -90) * mm});
            skLineSegment(sketch, "E95.MirrorCS", {"start": v(0, -90) * mm, "end": v(0, -120) * mm, "construction": true});
            skSolve(sketch);
        }
        {
            var Q0;
            Q0=makeQuery(id+"F16.imprint","IMPRINT",FACE,{"disambiguationData":[TD([[makeQuery(id+"F16.imprint","IMPRINT",EDGE,{"derivedFrom":sQuery(id+"F16.wireOp",EDGE,"E88.MirrorCS")}),1.0]])]});
            var Q1;
            Q1=makeQuery(id+"F16.imprint","IMPRINT",FACE,{"disambiguationData":[TD([[makeQuery(id+"F16.imprint","IMPRINT",EDGE,{"derivedFrom":sQuery(id+"F16.wireOp",EDGE,"E79.0")}),-1.0]])]});
            var Q2;
            Q2=makeQuery(id+"F16.imprint","IMPRINT",FACE,{"disambiguationData":[TD([[makeQuery(id+"F16.imprint","IMPRINT",EDGE,{"derivedFrom":sQuery(id+"F16.wireOp",EDGE,"E89.MirrorCS")}),1.0]])]});
            var Q3;
            Q3=makeQuery(id+"F2.opExtrude","CAP_FACE",FACE,{"disambiguationData":[OSD([sQuery(id+"F0.wireOp",EDGE,"E12"),sQuery(id+"F0.wireOp",EDGE,"E13"),sQuery(id+"F0.wireOp",EDGE,"E14"),sQuery(id+"F0.wireOp",EDGE,"E15"),sQuery(id+"F0.wireOp",EDGE,"E17.filletArc"),sQuery(id+"F0.wireOp",EDGE,"E18.filletArc"),sQuery(id+"F0.wireOp",EDGE,"E19.filletArc"),sQuery(id+"F0.wireOp",EDGE,"E20.filletArc"),sQuery(id+"F0.wireOp",EDGE,"E25.0"),sQuery(id+"F0.wireOp",EDGE,"E25.1"),sQuery(id+"F0.wireOp",EDGE,"E25.2"),sQuery(id+"F0.wireOp",EDGE,"E25.3"),sQuery(id+"F0.wireOp",EDGE,"E25.4"),sQuery(id+"F0.wireOp",EDGE,"E25.5"),sQuery(id+"F0.wireOp",EDGE,"E25.6"),sQuery(id+"F0.wireOp",EDGE,"E25.7")])],"isStart":false});
            extrude(context, id + "F17", {"entities" : qUnion([Q0, Q1, Q2]), "endBound" : BoundingType.UP_TO_SURFACE, "endBoundEntityFace" : qUnion([Q3]), "depth" : 25 * mm});
        }
    });
